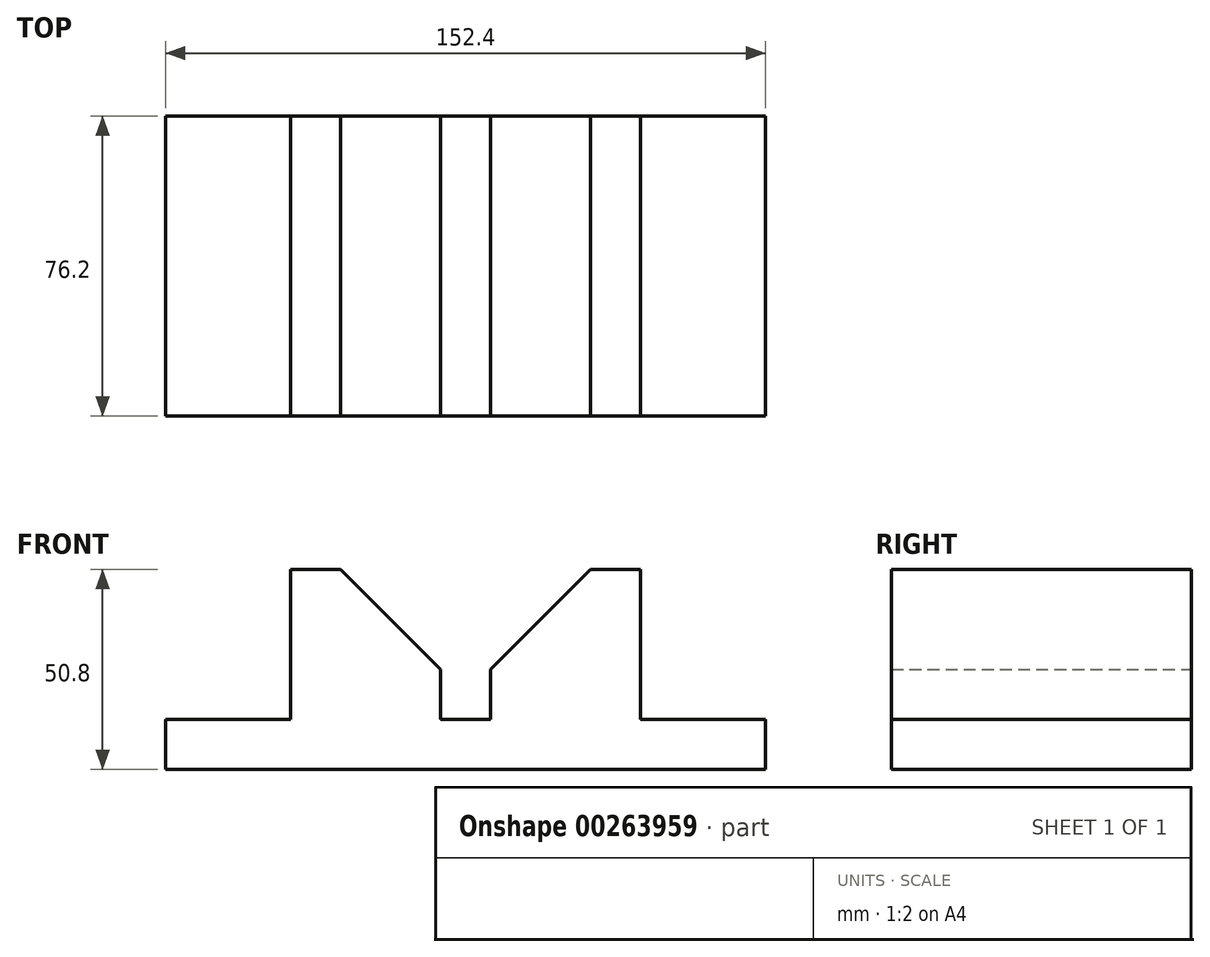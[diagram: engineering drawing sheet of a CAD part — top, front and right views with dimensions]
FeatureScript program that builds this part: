
annotation { "Feature Type Name" : "Feature", "Feature Type Description" : "" }
export const myFeature = defineFeature(function(context is Context, id is Id, definition is map)
    precondition{}
    {
        {
            var Q0;
            Q0=qCreatedBy(makeId("Front.planeOp"),FACE);
            var sketch = newSketch(context, id + "F0", { "sketchPlane" : qUnion([Q0])});
            skLineSegment(sketch, "E0", {"start": v(0, 0) * mm, "end": v(152.4, 0) * mm});
            skLineSegment(sketch, "E1", {"start": v(152.4, 0) * mm, "end": v(152.4, 12.7) * mm});
            skLineSegment(sketch, "E2", {"start": v(152.4, 12.7) * mm, "end": v(120.65, 12.7) * mm});
            skLineSegment(sketch, "E3", {"start": v(120.65, 12.7) * mm, "end": v(120.65, 50.8) * mm});
            skLineSegment(sketch, "E4", {"start": v(120.65, 50.8) * mm, "end": v(107.95, 50.8) * mm});
            skLineSegment(sketch, "E5", {"start": v(0, 0) * mm, "end": v(0, 12.7) * mm});
            skLineSegment(sketch, "E6", {"start": v(0, 12.7) * mm, "end": v(31.75, 12.7) * mm});
            skLineSegment(sketch, "E7", {"start": v(31.75, 12.7) * mm, "end": v(31.75, 50.8) * mm});
            skLineSegment(sketch, "E8", {"start": v(31.75, 50.8) * mm, "end": v(44.45, 50.8) * mm});
            skLineSegment(sketch, "E9", {"start": v(31.75, 12.7) * mm, "end": v(69.85, 12.7) * mm, "construction": true});
            skLineSegment(sketch, "E10", {"start": v(69.85, 12.7) * mm, "end": v(82.55, 12.7) * mm, "construction": true});
            skLineSegment(sketch, "E11", {"start": v(82.55, 12.7) * mm, "end": v(82.55, 25.4) * mm});
            skLineSegment(sketch, "E12", {"start": v(82.55, 25.4) * mm, "end": v(69.85, 25.4) * mm, "construction": true});
            skLineSegment(sketch, "E13", {"start": v(69.85, 25.4) * mm, "end": v(69.85, 12.7) * mm, "construction": true});
            skLineSegment(sketch, "E14", {"start": v(69.85, 12.7) * mm, "end": v(82.55, 12.7) * mm});
            skLineSegment(sketch, "E15", {"start": v(82.55, 25.4) * mm, "end": v(107.95, 50.8) * mm});
            skLineSegment(sketch, "E16", {"start": v(69.85, 12.7) * mm, "end": v(69.85, 25.4) * mm});
            skLineSegment(sketch, "E17", {"start": v(44.45, 50.8) * mm, "end": v(69.85, 25.4) * mm});
            skSolve(sketch);
        }
        {
            var Q0;
            Q0=makeQuery(id+"F0.imprint","IMPRINT",FACE,{"disambiguationData":[TD([[makeQuery(id+"F0.imprint","IMPRINT",EDGE,{"derivedFrom":sQuery(id+"F0.wireOp",EDGE,"E0")}),1.0]])]});
            extrude(context, id + "F1", {"entities" : qUnion([Q0]), "depth" : 76.2 * mm});
        }
    });
